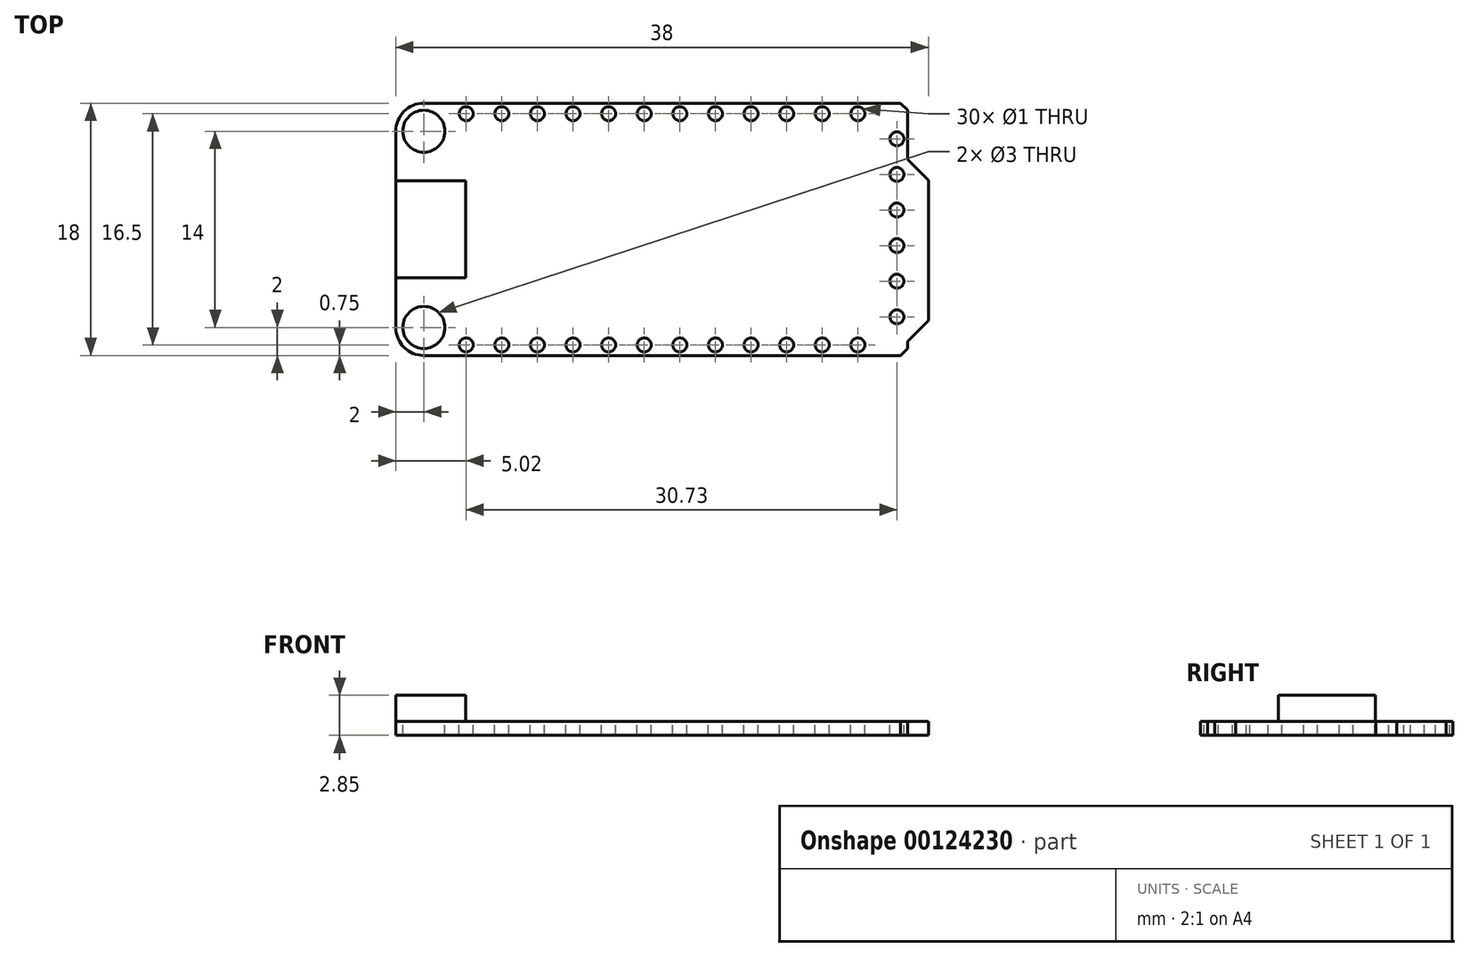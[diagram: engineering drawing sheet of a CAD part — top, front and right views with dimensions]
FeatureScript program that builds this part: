
annotation { "Feature Type Name" : "Feature", "Feature Type Description" : "" }
export const myFeature = defineFeature(function(context is Context, id is Id, definition is map)
    precondition{}
    {
        {
            var Q0;
            Q0=qCreatedBy(makeId("Top.planeOp"),FACE);
            var sketch = newSketch(context, id + "F0", { "sketchPlane" : qUnion([Q0])});
            skLineSegment(sketch, "E0.bottom", {"start": v(17.5, 9) * mm, "end": v(-19, 9) * mm});
            skLineSegment(sketch, "E0.top", {"start": v(17.5, -9) * mm, "end": v(-19, -9) * mm});
            skLineSegment(sketch, "E0.left", {"start": v(19, 3.5) * mm, "end": v(19, -6.5) * mm});
            skLineSegment(sketch, "E0.right", {"start": v(-19, 9) * mm, "end": v(-19, -9) * mm});
            skPoint(sketch, "E0.middle", {"position": v(0, 0) * mm});
            skLineSegment(sketch, "E1", {"start": v(17.5, 9) * mm, "end": v(17.5, 5) * mm});
            skLineSegment(sketch, "E2", {"start": v(17.5, -8) * mm, "end": v(19, -6.5) * mm});
            skLineSegment(sketch, "E3", {"start": v(17.5, 5) * mm, "end": v(19, 3.5) * mm});
            skPoint(sketch, "E4.orphan", {"position": v(19, 9) * mm});
            skPoint(sketch, "E5.orphan", {"position": v(19, -9) * mm});
            skLineSegment(sketch, "E6.trimOffspring", {"start": v(17.5, -8) * mm, "end": v(17.5, -9) * mm});
            skSolve(sketch);
        }
        {
            var Q0;
            Q0=makeQuery(id+"F0.imprint","IMPRINT",FACE,{"disambiguationData":[TD([[makeQuery(id+"F0.imprint","IMPRINT",EDGE,{"derivedFrom":sQuery(id+"F0.wireOp",EDGE,"E0.bottom")}),1.0]])]});
            extrude(context, id + "F1", {"entities" : qUnion([Q0]), "depth" : 1 * mm});
        }
        {
            var Q0;
            Q0=makeQuery(id+"F1.opExtrude","CAP_FACE",FACE,{"disambiguationData":[OSD([sQuery(id+"F0.wireOp",EDGE,"E0.bottom"),sQuery(id+"F0.wireOp",EDGE,"E0.top"),sQuery(id+"F0.wireOp",EDGE,"E0.left"),sQuery(id+"F0.wireOp",EDGE,"E0.right"),sQuery(id+"F0.wireOp",EDGE,"E1"),sQuery(id+"F0.wireOp",EDGE,"E2"),sQuery(id+"F0.wireOp",EDGE,"E3"),sQuery(id+"F0.wireOp",EDGE,"E6.trimOffspring")])],"isStart":false});
            var sketch = newSketch(context, id + "F2", { "sketchPlane" : qUnion([Q0])});
            skCircle(sketch, "E7", {"center": v(13.96, -8.25) * mm, "radius": 0.5 * mm});
            skCircle(sketch, "E8.1.0.0", {"center": v(11.42, -8.25) * mm, "radius": 0.5 * mm});
            skCircle(sketch, "E8.2.0.0", {"center": v(8.88, -8.25) * mm, "radius": 0.5 * mm});
            skCircle(sketch, "E8.3.0.0", {"center": v(6.34, -8.25) * mm, "radius": 0.5 * mm});
            skCircle(sketch, "E8.4.0.0", {"center": v(3.8, -8.25) * mm, "radius": 0.5 * mm});
            skCircle(sketch, "E8.5.0.0", {"center": v(1.26, -8.25) * mm, "radius": 0.5 * mm});
            skCircle(sketch, "E8.6.0.0", {"center": v(-1.28, -8.25) * mm, "radius": 0.5 * mm});
            skCircle(sketch, "E8.7.0.0", {"center": v(-3.82, -8.25) * mm, "radius": 0.5 * mm});
            skCircle(sketch, "E8.8.0.0", {"center": v(-6.36, -8.25) * mm, "radius": 0.5 * mm});
            skCircle(sketch, "E8.9.0.0", {"center": v(-8.9, -8.25) * mm, "radius": 0.5 * mm});
            skCircle(sketch, "E8.10.0.0", {"center": v(-11.44, -8.25) * mm, "radius": 0.5 * mm});
            skCircle(sketch, "E8.11.0.0", {"center": v(-13.98, -8.25) * mm, "radius": 0.5 * mm});
            skLineSegment(sketch, "E8.direction1", {"start": v(13.96, -8.25) * mm, "end": v(11.42, -8.25) * mm, "construction": true});
            skLineSegment(sketch, "E9", {"start": v(0, 0) * mm, "end": v(-19, 0) * mm, "construction": true});
            skCircle(sketch, "E10.MirrorC", {"center": v(13.96, 8.25) * mm, "radius": 0.5 * mm});
            skCircle(sketch, "E11.MirrorC", {"center": v(11.42, 8.25) * mm, "radius": 0.5 * mm});
            skCircle(sketch, "E12.MirrorC", {"center": v(8.88, 8.25) * mm, "radius": 0.5 * mm});
            skCircle(sketch, "E13.MirrorC", {"center": v(-1.28, 8.25) * mm, "radius": 0.5 * mm});
            skCircle(sketch, "E14.MirrorC", {"center": v(1.26, 8.25) * mm, "radius": 0.5 * mm});
            skCircle(sketch, "E15.MirrorC", {"center": v(-6.36, 8.25) * mm, "radius": 0.5 * mm});
            skCircle(sketch, "E16.MirrorC", {"center": v(-8.9, 8.25) * mm, "radius": 0.5 * mm});
            skCircle(sketch, "E17.MirrorC", {"center": v(-3.82, 8.25) * mm, "radius": 0.5 * mm});
            skCircle(sketch, "E18.MirrorC", {"center": v(3.8, 8.25) * mm, "radius": 0.5 * mm});
            skCircle(sketch, "E19.MirrorC", {"center": v(6.34, 8.25) * mm, "radius": 0.5 * mm});
            skCircle(sketch, "E20.MirrorC", {"center": v(-13.98, 8.25) * mm, "radius": 0.5 * mm});
            skCircle(sketch, "E21.MirrorC", {"center": v(-11.44, 8.25) * mm, "radius": 0.5 * mm});
            skCircle(sketch, "E22.MirrorC", {"center": v(16.75, 6.46) * mm, "radius": 0.5 * mm});
            skCircle(sketch, "E23.1.0.0", {"center": v(16.75, 3.92) * mm, "radius": 0.5 * mm});
            skCircle(sketch, "E23.2.0.0", {"center": v(16.75, 1.38) * mm, "radius": 0.5 * mm});
            skCircle(sketch, "E23.3.0.0", {"center": v(16.75, -1.16) * mm, "radius": 0.5 * mm});
            skCircle(sketch, "E23.4.0.0", {"center": v(16.75, -3.7) * mm, "radius": 0.5 * mm});
            skCircle(sketch, "E23.5.0.0", {"center": v(16.75, -6.24) * mm, "radius": 0.5 * mm});
            skLineSegment(sketch, "E23.direction1", {"start": v(16.75, 6.46) * mm, "end": v(16.75, 3.92) * mm, "construction": true});
            skSolve(sketch);
        }
        {
            var Q0;
            Q0 = qSketchRegion(id + "F2", true);
            extrude(context, id + "F3", {"entities" : qUnion([Q0]), "operationType" : NewBodyOperationType.REMOVE, "endBound" : BoundingType.THROUGH_ALL, "oppositeDirection" : true, "depth" : 25 * mm});
        }
        {
            var Q0;
            Q0=makeQuery(id+"F1.opExtrude","SWEPT_EDGE",EDGE,{"disambiguationData":[OSD([sQuery(id+"F0.wireOp",EDGE,"E0.bottom"),sQuery(id+"F0.wireOp",EDGE,"E1")])]});
            var Q1;
            Q1=makeQuery(id+"F1.opExtrude","SWEPT_EDGE",EDGE,{"disambiguationData":[OSD([sQuery(id+"F0.wireOp",EDGE,"E0.top"),sQuery(id+"F0.wireOp",EDGE,"E6.trimOffspring")])]});
            chamfer(context, id + "F4", {"entities" : qUnion([Q0, Q1]), "width" : 0.5 * mm, "tangentPropagation" : true});
        }
        {
            var Q0;
            Q0=makeQuery(id+"F1.opExtrude","SWEPT_EDGE",EDGE,{"disambiguationData":[OSD([sQuery(id+"F0.wireOp",EDGE,"E0.top"),sQuery(id+"F0.wireOp",EDGE,"E0.right")])]});
            var Q1;
            Q1=makeQuery(id+"F1.opExtrude","SWEPT_EDGE",EDGE,{"disambiguationData":[OSD([sQuery(id+"F0.wireOp",EDGE,"E0.bottom"),sQuery(id+"F0.wireOp",EDGE,"E0.right")])]});
            fillet(context, id + "F5", {"entities" : qUnion([Q0, Q1]), "radius" : 2 * mm, "tangentPropagation" : true, "allowEdgeOverflow" : false});
        }
        {
            var Q0;
            Q0=makeQuery(id+"F1.opExtrude","CAP_FACE",FACE,{"disambiguationData":[OSD([sQuery(id+"F0.wireOp",EDGE,"E0.bottom"),sQuery(id+"F0.wireOp",EDGE,"E0.top"),sQuery(id+"F0.wireOp",EDGE,"E0.left"),sQuery(id+"F0.wireOp",EDGE,"E0.right"),sQuery(id+"F0.wireOp",EDGE,"E1"),sQuery(id+"F0.wireOp",EDGE,"E2"),sQuery(id+"F0.wireOp",EDGE,"E3"),sQuery(id+"F0.wireOp",EDGE,"E6.trimOffspring")])],"isStart":false});
            var sketch = newSketch(context, id + "F6", { "sketchPlane" : qUnion([Q0])});
            skCircle(sketch, "E24", {"center": v(-17, 7) * mm, "radius": 1.5 * mm});
            skCircle(sketch, "E25", {"center": v(-17, -7) * mm, "radius": 1.5 * mm});
            skSolve(sketch);
        }
        {
            var Q0;
            Q0 = qSketchRegion(id + "F6", true);
            extrude(context, id + "F7", {"entities" : qUnion([Q0]), "operationType" : NewBodyOperationType.REMOVE, "endBound" : BoundingType.THROUGH_ALL, "oppositeDirection" : true, "depth" : 25 * mm});
        }
        {
            var Q0;
            Q0=makeQuery(id+"F1.opExtrude","CAP_FACE",FACE,{"disambiguationData":[OSD([sQuery(id+"F0.wireOp",EDGE,"E0.bottom"),sQuery(id+"F0.wireOp",EDGE,"E0.top"),sQuery(id+"F0.wireOp",EDGE,"E0.left"),sQuery(id+"F0.wireOp",EDGE,"E0.right"),sQuery(id+"F0.wireOp",EDGE,"E1"),sQuery(id+"F0.wireOp",EDGE,"E2"),sQuery(id+"F0.wireOp",EDGE,"E3"),sQuery(id+"F0.wireOp",EDGE,"E6.trimOffspring")])],"isStart":false});
            var sketch = newSketch(context, id + "F8", { "sketchPlane" : qUnion([Q0])});
            skLineSegment(sketch, "E26", {"start": v(0, 0) * mm, "end": v(-19, 0) * mm, "construction": true});
            skLineSegment(sketch, "E27.bottom", {"start": v(-19, 3.45) * mm, "end": v(-14, 3.45) * mm});
            skLineSegment(sketch, "E27.top", {"start": v(-19, -3.45) * mm, "end": v(-14, -3.45) * mm});
            skLineSegment(sketch, "E27.left", {"start": v(-19, 3.45) * mm, "end": v(-19, -3.45) * mm});
            skLineSegment(sketch, "E27.right", {"start": v(-14, 3.45) * mm, "end": v(-14, -3.45) * mm});
            skSolve(sketch);
        }
        {
            var Q0;
            Q0=makeQuery(id+"F8.imprint","IMPRINT",FACE,{"disambiguationData":[TD([[makeQuery(id+"F8.imprint","IMPRINT",EDGE,{"derivedFrom":sQuery(id+"F8.wireOp",EDGE,"E27.bottom")}),-1.0]])]});
            extrude(context, id + "F9", {"entities" : qUnion([Q0]), "operationType" : NewBodyOperationType.ADD, "depth" : 1.85 * mm});
        }
    });
